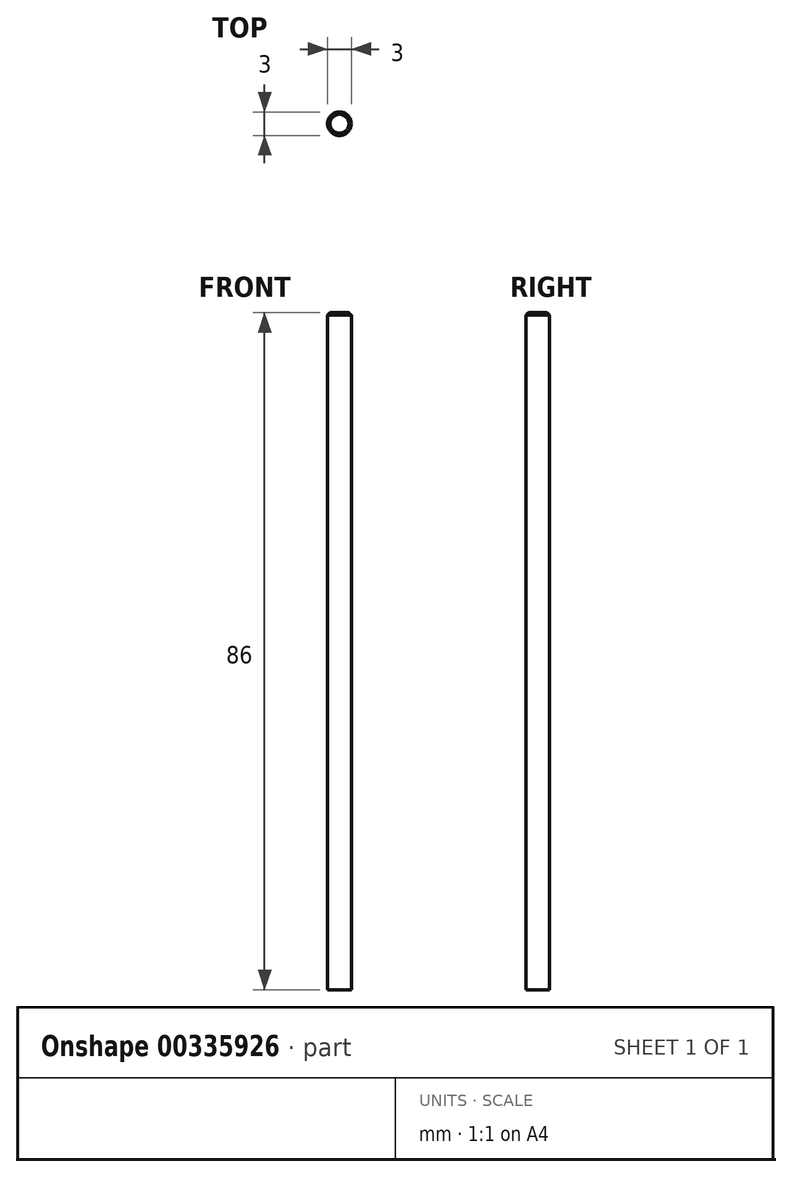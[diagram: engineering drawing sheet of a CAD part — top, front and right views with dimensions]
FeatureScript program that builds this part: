
annotation { "Feature Type Name" : "Feature", "Feature Type Description" : "" }
export const myFeature = defineFeature(function(context is Context, id is Id, definition is map)
    precondition{}
    {
        {
            var Q0;
            Q0=qCreatedBy(makeId("Top.planeOp"),FACE);
            var sketch = newSketch(context, id + "F0", { "sketchPlane" : qUnion([Q0])});
            skCircle(sketch, "E0", {"center": v(0, 0) * mm, "radius": 1.5 * mm});
            skSolve(sketch);
        }
        {
            var Q0;
            Q0 = qSketchRegion(id + "F0", true);
            extrude(context, id + "F1", {"entities" : qUnion([Q0]), "endBound" : BoundingType.SYMMETRIC, "depth" : 86 * mm});
        }
        {
            var Q0;
            Q0=makeQuery(id+"F1.opExtrude","CAP_EDGE",EDGE,{"disambiguationData":[OSD([sQuery(id+"F0.wireOp",EDGE,"E0")])],"isStart":false});
            chamfer(context, id + "F2", {"entities" : qUnion([Q0]), "width" : 0.3 * mm, "tangentPropagation" : true});
        }
    });
